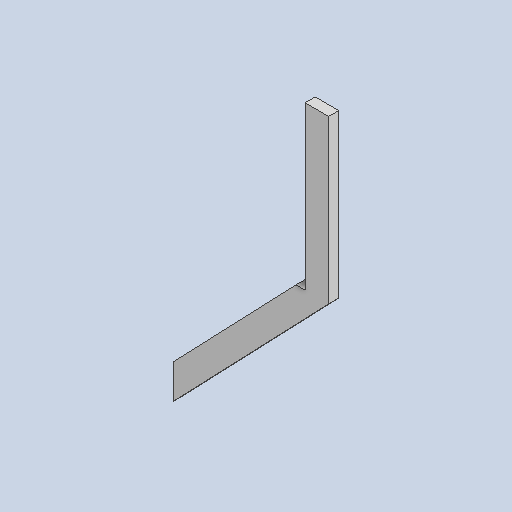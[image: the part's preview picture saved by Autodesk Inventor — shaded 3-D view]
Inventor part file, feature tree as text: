
AUTODESK INVENTOR PART (.ipt)
format: ipt  version: 2025 (Build 290162000, 162)  size: 82,944 bytes
history: native  units: in
note: dims shown in document units (in); Inventor stores cm internally (conversion verified against a paired STEP export)
features: other x3, sketch x1
ambient origin geometry x8: Origin, YZ Plane, XZ Plane, XY Plane, X Axis, Y Axis, Z Axis, Center Point
bodies: Solid1 (feature_tree)
feature tree (4):
  other  "back_side.ipt"
  other  "Solid1::back_side.ipt"
  other  "TaggingFeature1"
  sketch  "Sketch1"  dims[d0=0.3937in]
